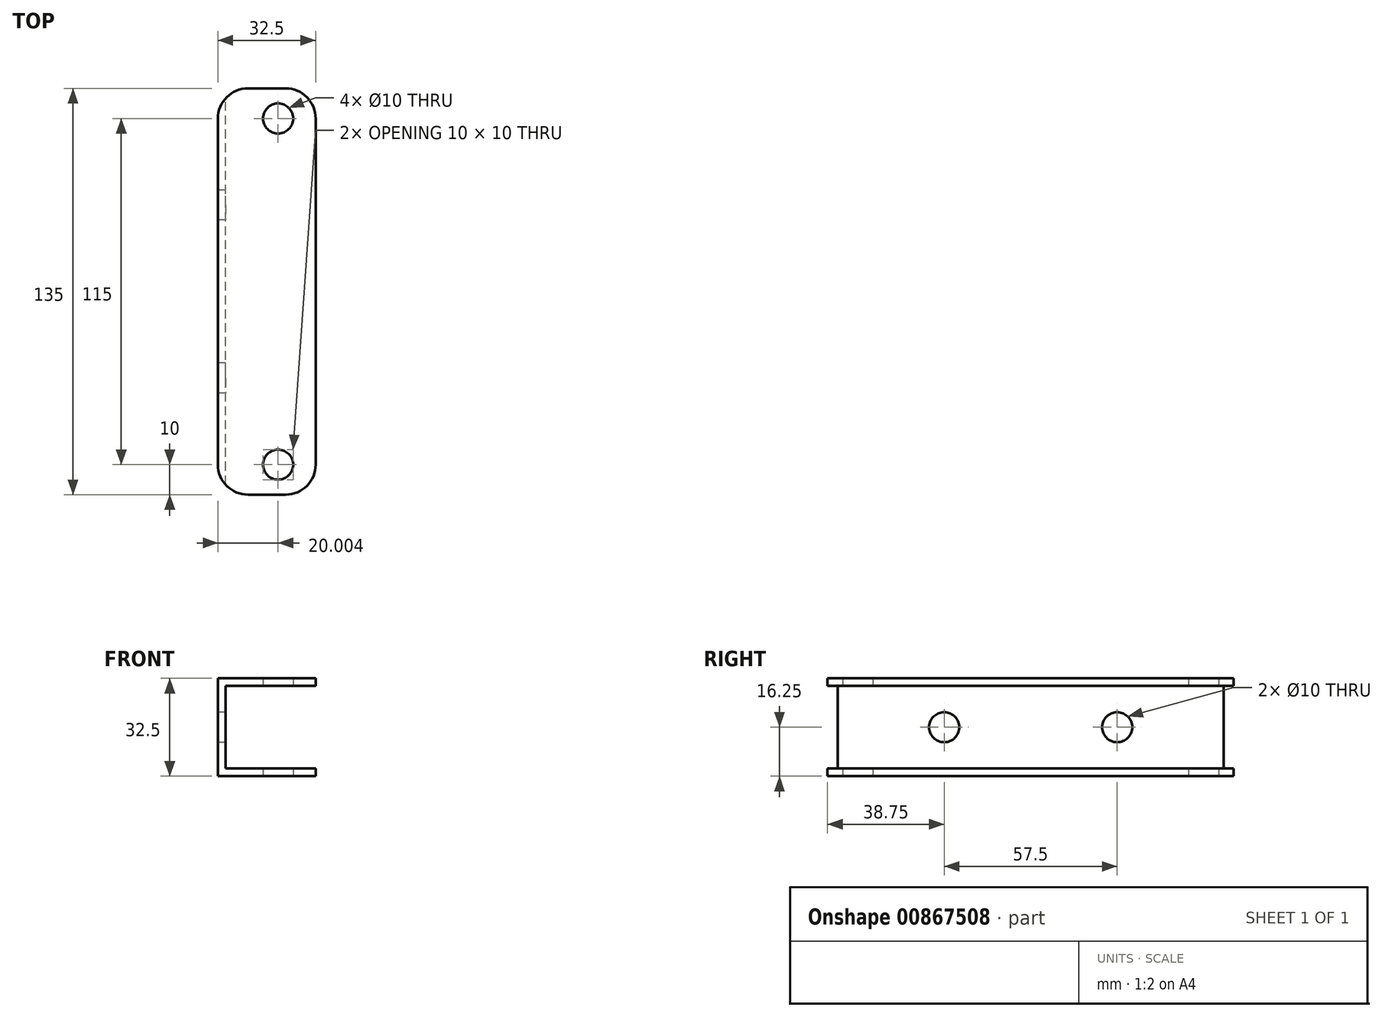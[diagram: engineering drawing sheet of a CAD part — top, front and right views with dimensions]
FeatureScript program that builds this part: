
annotation { "Feature Type Name" : "Feature", "Feature Type Description" : "" }
export const myFeature = defineFeature(function(context is Context, id is Id, definition is map)
    precondition{}
    {
        {
            var Q0;
            Q0=qCreatedBy(makeId("Front.planeOp"),FACE);
            var sketch = newSketch(context, id + "F0", { "sketchPlane" : qUnion([Q0])});
            skLineSegment(sketch, "E0.bottom", {"start": v(-74.99, 0) * mm, "end": v(-42.49, 0) * mm});
            skLineSegment(sketch, "E0.top", {"start": v(-74.99, 32.5) * mm, "end": v(-42.49, 32.5) * mm});
            skLineSegment(sketch, "E0.left", {"start": v(-74.99, 0) * mm, "end": v(-74.99, 32.5) * mm});
            skLineSegment(sketch, "E0.right", {"start": v(-42.49, 0) * mm, "end": v(-42.49, 2.5) * mm});
            skLineSegment(sketch, "E1.top", {"start": v(-42.49, 2.5) * mm, "end": v(-72.49, 2.5) * mm});
            skLineSegment(sketch, "E2.top", {"start": v(-42.49, 30) * mm, "end": v(-72.49, 30) * mm});
            skLineSegment(sketch, "E3.trimOffspring", {"start": v(-42.49, 30) * mm, "end": v(-42.49, 32.5) * mm});
            skPoint(sketch, "E2.left.start.orphan", {"position": v(-42.49, 16.25) * mm});
            skLineSegment(sketch, "E4", {"start": v(-72.49, 30) * mm, "end": v(-72.49, 2.5) * mm});
            skSolve(sketch);
        }
        {
            var Q0;
            Q0=qCreatedBy(makeId("Top.planeOp"),FACE);
            var sketch = newSketch(context, id + "F1", { "sketchPlane" : qUnion([Q0])});
            skLineSegment(sketch, "E5.0", {"start": v(0, -150) * mm, "end": v(-82.52, -150) * mm, "construction": true});
            skLineSegment(sketch, "E6.bottom", {"start": v(-59.99, -290) * mm, "end": v(-54.99, -290) * mm});
            skCircle(sketch, "E7", {"center": v(-54.99, -10) * mm, "radius": 5 * mm});
            skCircle(sketch, "E8", {"center": v(-54.99, -290) * mm, "radius": 5 * mm});
            skCircle(sketch, "E9", {"center": v(-54.99, -260) * mm, "radius": 5 * mm});
            skCircle(sketch, "E10", {"center": v(-54.99, -125) * mm, "radius": 5 * mm});
            skLineSegment(sketch, "E11", {"start": v(-54.99, -10) * mm, "end": v(-54.99, -150) * mm, "construction": true});
            skSolve(sketch);
        }
        {
            var Q0;
            Q0=makeQuery(id+"F0.imprint","IMPRINT",FACE,{"disambiguationData":[TD([[makeQuery(id+"F0.imprint","IMPRINT",EDGE,{"derivedFrom":sQuery(id+"F0.wireOp",EDGE,"E0.bottom")}),1.0]])]});
            extrude(context, id + "F2", {"entities" : qUnion([Q0]), "depth" : 135 * mm, "offsetDistance" : 25 * mm});
        }
        {
            var Q0;
            {var subQ0=sQuery(id+"F1.wireOp",EDGE,"E8");Q0=makeQuery(id+"F1.imprint","IMPRINT",FACE,{"disambiguationData":[TD([[makeQuery(id+"F1.imprint","IMPRINT",EDGE,{"disambiguationData":[TD([[makeQuery(id+"F1.imprint","IMPRINT",VERTEX,{"derivedFrom":subQ0}),-1.0]])],"derivedFrom":subQ0}),1.0]])]});}
            var Q1;
            Q1=makeQuery(id+"F1.imprint","IMPRINT",FACE,{"disambiguationData":[TD([[makeQuery(id+"F1.imprint","IMPRINT",EDGE,{"derivedFrom":sQuery(id+"F1.wireOp",EDGE,"E9")}),1.0]])]});
            var Q2;
            Q2=makeQuery(id+"F1.imprint","IMPRINT",FACE,{"disambiguationData":[TD([[makeQuery(id+"F1.imprint","IMPRINT",EDGE,{"derivedFrom":sQuery(id+"F1.wireOp",EDGE,"E10")}),1.0]])]});
            var Q3;
            Q3=makeQuery(id+"F1.imprint","IMPRINT",FACE,{"disambiguationData":[TD([[makeQuery(id+"F1.imprint","IMPRINT",EDGE,{"derivedFrom":sQuery(id+"F1.wireOp",EDGE,"E7")}),1.0]])]});
            extrude(context, id + "F3", {"entities" : qUnion([Q0, Q1, Q2, Q3]), "operationType" : NewBodyOperationType.REMOVE, "depth" : 46 * mm, "offsetDistance" : 25 * mm});
        }
        {
            var Q0;
            Q0=makeQuery(id+"F2.opExtrude","CAP_EDGE",EDGE,{"disambiguationData":[OSD([sQuery(id+"F0.wireOp",EDGE,"E0.right")])],"isStart":true});
            var Q1;
            Q1=makeQuery(id+"F2.opExtrude","CAP_EDGE",EDGE,{"disambiguationData":[OSD([sQuery(id+"F0.wireOp",EDGE,"E3.trimOffspring")])],"isStart":true});
            var Q2;
            Q2=makeQuery(id+"F2.opExtrude","CAP_EDGE",EDGE,{"disambiguationData":[OSD([sQuery(id+"F0.wireOp",EDGE,"E3.trimOffspring")])],"isStart":false});
            var Q3;
            Q3=makeQuery(id+"F2.opExtrude","CAP_EDGE",EDGE,{"disambiguationData":[OSD([sQuery(id+"F0.wireOp",EDGE,"E0.right")])],"isStart":false});
            var Q4;
            Q4=makeQuery(id+"F2.opExtrude","CAP_EDGE",EDGE,{"disambiguationData":[OSD([sQuery(id+"F0.wireOp",EDGE,"E0.left")])],"isStart":true});
            var Q5;
            Q5=makeQuery(id+"F2.opExtrude","CAP_EDGE",EDGE,{"disambiguationData":[OSD([sQuery(id+"F0.wireOp",EDGE,"E0.left")])],"isStart":false});
            fillet(context, id + "F4", {"entities" : qUnion([Q0, Q1, Q2, Q3, Q4, Q5]), "radius" : 10 * mm, "tangentPropagation" : true, "allowEdgeOverflow" : false});
        }
        {
            var Q0;
            Q0=makeQuery(id+"F2.opExtrude","SWEPT_FACE",FACE,{"disambiguationData":[OSD([sQuery(id+"F0.wireOp",EDGE,"E0.left")])]});
            cPlane(context, id + "F5", {"entities" : qUnion([Q0]), "cplaneType" : CPlaneType.OFFSET, "offset" : 0 * mm, "width" : 150 * mm, "height" : 150 * mm});
        }
        {
            var Q0;
            Q0=qCreatedBy(id+"F5.planeOp",FACE);
            var sketch = newSketch(context, id + "F6", { "sketchPlane" : qUnion([Q0])});
            skLineSegment(sketch, "E12.bottom", {"start": v(10, 32.5) * mm, "end": v(67.5, 32.5) * mm});
            skLineSegment(sketch, "E12.top", {"start": v(10, 0) * mm, "end": v(67.5, 0) * mm});
            skLineSegment(sketch, "E12.left", {"start": v(10, 32.5) * mm, "end": v(10, 0) * mm});
            skLineSegment(sketch, "E12.right", {"start": v(67.5, 32.5) * mm, "end": v(67.5, 0) * mm});
            skLineSegment(sketch, "E13.bottom", {"start": v(67.5, 0) * mm, "end": v(38.75, 0) * mm});
            skLineSegment(sketch, "E13.top", {"start": v(67.5, 16.25) * mm, "end": v(38.75, 16.25) * mm});
            skLineSegment(sketch, "E13.left", {"start": v(67.5, 0) * mm, "end": v(67.5, 16.25) * mm});
            skLineSegment(sketch, "E13.right", {"start": v(38.75, 0) * mm, "end": v(38.75, 16.25) * mm});
            skLineSegment(sketch, "E14", {"start": v(67.5, 16.25) * mm, "end": v(96.25, 16.25) * mm});
            skCircle(sketch, "E15", {"center": v(38.75, 16.25) * mm, "radius": 5 * mm});
            skCircle(sketch, "E16", {"center": v(96.25, 16.25) * mm, "radius": 5 * mm});
            skSolve(sketch);
        }
        {
            var Q0;
            {var subQ0=sQuery(id+"F6.wireOp",EDGE,"E13.right");var subQ1=sQuery(id+"F6.wireOp",EDGE,"E13.top");var subQ2=makeQuery(id+"F6.imprint","INTERSECT",VERTEX,{"derivedFrom":[subQ1,subQ0]});Q0=makeQuery(id+"F6.imprint","IMPRINT",FACE,{"disambiguationData":[TD([[makeQuery(id+"F6.imprint","IMPRINT",EDGE,{"disambiguationData":[TD([[subQ2,1.0]])],"derivedFrom":subQ1}),-1.0]])]});}
            var Q1;
            {var subQ0=sQuery(id+"F6.wireOp",EDGE,"E13.right");var subQ1=sQuery(id+"F6.wireOp",EDGE,"E13.top");var subQ2=makeQuery(id+"F6.imprint","INTERSECT",VERTEX,{"derivedFrom":[subQ1,subQ0]});Q1=makeQuery(id+"F6.imprint","IMPRINT",FACE,{"disambiguationData":[TD([[makeQuery(id+"F6.imprint","IMPRINT",EDGE,{"disambiguationData":[TD([[subQ2,1.0]])],"derivedFrom":subQ1}),1.0]])]});}
            var Q2;
            Q2=makeQuery(id+"F6.imprint","IMPRINT",FACE,{"disambiguationData":[TD([[makeQuery(id+"F6.imprint","IMPRINT",EDGE,{"derivedFrom":sQuery(id+"F6.wireOp",EDGE,"E16")}),1.0]])]});
            extrude(context, id + "F7", {"entities" : qUnion([Q0, Q1, Q2]), "operationType" : NewBodyOperationType.REMOVE, "oppositeDirection" : true, "depth" : 25 * mm, "offsetDistance" : 25 * mm});
        }
    });
